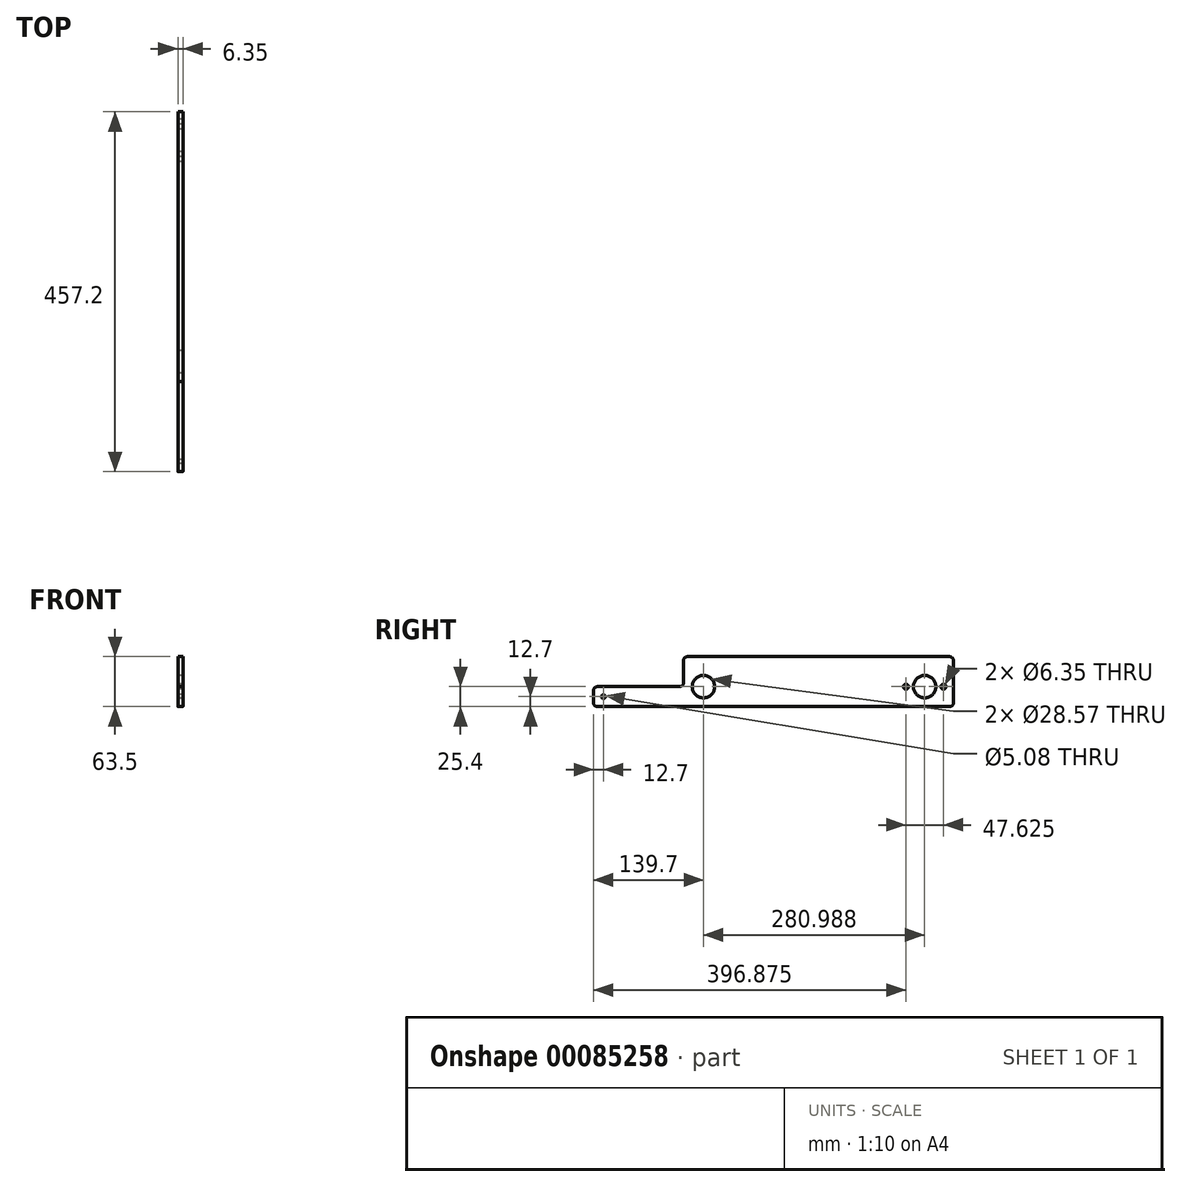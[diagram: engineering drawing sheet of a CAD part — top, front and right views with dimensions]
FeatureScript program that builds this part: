
annotation { "Feature Type Name" : "Feature", "Feature Type Description" : "" }
export const myFeature = defineFeature(function(context is Context, id is Id, definition is map)
    precondition{}
    {
        {
            var Q0;
            Q0=qCreatedBy(makeId("Right.planeOp"),FACE);
            var sketch = newSketch(context, id + "F0", { "sketchPlane" : qUnion([Q0])});
            skLineSegment(sketch, "E0.top", {"start": v(-228.6, 63.5) * mm, "end": v(228.6, 63.5) * mm});
            skLineSegment(sketch, "E0.right", {"start": v(228.6, -63.5) * mm, "end": v(228.6, 63.5) * mm});
            skPoint(sketch, "E0.middle", {"position": v(0, 0) * mm});
            skCircle(sketch, "E1", {"center": v(192.09, 0) * mm, "radius": 14.29 * mm});
            skCircle(sketch, "E2", {"center": v(168.28, 0) * mm, "radius": 3.18 * mm});
            skCircle(sketch, "E3", {"center": v(215.9, 0) * mm, "radius": 3.18 * mm});
            skLineSegment(sketch, "E4", {"start": v(-88.9, 0) * mm, "end": v(228.6, 0) * mm});
            skCircle(sketch, "E5", {"center": v(-88.9, 0) * mm, "radius": 14.29 * mm});
            skLineSegment(sketch, "E6", {"start": v(228.6, -25.4) * mm, "end": v(-228.6, -25.4) * mm});
            skLineSegment(sketch, "E7", {"start": v(-114.3, 63.5) * mm, "end": v(-114.3, -63.5) * mm});
            skLineSegment(sketch, "E8", {"start": v(-228.6, 63.5) * mm, "end": v(-228.6, -63.5) * mm});
            skLineSegment(sketch, "E9", {"start": v(228.6, 38.1) * mm, "end": v(-114.3, 38.1) * mm});
            skLineSegment(sketch, "E10", {"start": v(-228.6, 0) * mm, "end": v(-114.3, 0) * mm});
            skCircle(sketch, "E11", {"center": v(-215.9, -12.7) * mm, "radius": 2.54 * mm});
            skSolve(sketch);
        }
        {
            var Q0;
            {var subQ5=sQuery(id+"F0.wireOp",EDGE,"E10");Q0=makeQuery(id+"F0.imprint","IMPRINT",FACE,{"disambiguationData":[TD([[makeQuery(id+"F0.imprint","IMPRINT",EDGE,{"derivedFrom":subQ5}),-1.0]])]});}
            var Q1;
            Q1=makeQuery(id+"F0.imprint","IMPRINT",FACE,{"disambiguationData":[TD([[makeQuery(id+"F0.imprint","IMPRINT",EDGE,{"derivedFrom":sQuery(id+"F0.wireOp",EDGE,"E5")}),-1.0]])]});
            extrude(context, id + "F1", {"entities" : qUnion([Q0, Q1]), "depth" : 6.35 * mm});
        }
        {
            var Q0;
            Q0=makeQuery(id+"F1.opExtrude","SWEPT_EDGE",EDGE,{"disambiguationData":[OSD([sQuery(id+"F0.wireOp",EDGE,"E7"),sQuery(id+"F0.wireOp",EDGE,"E10")])]});
            var Q1;
            Q1=makeQuery(id+"F1.opExtrude","SWEPT_EDGE",EDGE,{"disambiguationData":[OSD([sQuery(id+"F0.wireOp",EDGE,"E7"),sQuery(id+"F0.wireOp",EDGE,"E9")])]});
            var Q2;
            Q2=makeQuery(id+"F1.opExtrude","SWEPT_EDGE",EDGE,{"disambiguationData":[OSD([sQuery(id+"F0.wireOp",EDGE,"E8"),sQuery(id+"F0.wireOp",EDGE,"E10")])]});
            var Q3;
            Q3=makeQuery(id+"F1.opExtrude","SWEPT_EDGE",EDGE,{"disambiguationData":[OSD([sQuery(id+"F0.wireOp",EDGE,"E6"),sQuery(id+"F0.wireOp",EDGE,"E8")])]});
            var Q4;
            Q4=makeQuery(id+"F1.opExtrude","SWEPT_EDGE",EDGE,{"disambiguationData":[OSD([sQuery(id+"F0.wireOp",EDGE,"E0.right"),sQuery(id+"F0.wireOp",EDGE,"E9")])]});
            var Q5;
            Q5=makeQuery(id+"F1.opExtrude","SWEPT_EDGE",EDGE,{"disambiguationData":[OSD([sQuery(id+"F0.wireOp",EDGE,"E0.right"),sQuery(id+"F0.wireOp",EDGE,"E6")])]});
            fillet(context, id + "F2", {"entities" : qUnion([Q0, Q1, Q2, Q3, Q4, Q5]), "radius" : 5.08 * mm, "tangentPropagation" : true, "allowEdgeOverflow" : false});
        }
    });
